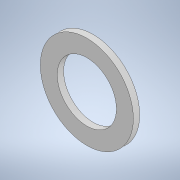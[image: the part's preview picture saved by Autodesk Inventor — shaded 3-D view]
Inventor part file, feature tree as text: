
AUTODESK INVENTOR PART (.ipt)
format: ipt  version: 2021 (Build 250183000, 183)  size: 105,472 bytes
history: native  units: mm
features: extrude x2, sketch x2
ambient origin geometry x8: Origin, YZ Plane, XZ Plane, XY Plane, X Axis, Y Axis, Z Axis, Center Point
bodies: Solid1 (feature_tree)
feature tree (4):
  extrude  "Extrusion1"  Depth=22.0mm
  extrude  "Extrusion2"  Depth=10.0mm
  sketch  "Sketch1"  dims[d0=9.0mm d1=22.0mm]
  sketch  "Sketch2"  dims[d2=1.5mm d3=0.0mm d4=14.0mm d5=10.0mm d6=0.0mm]
